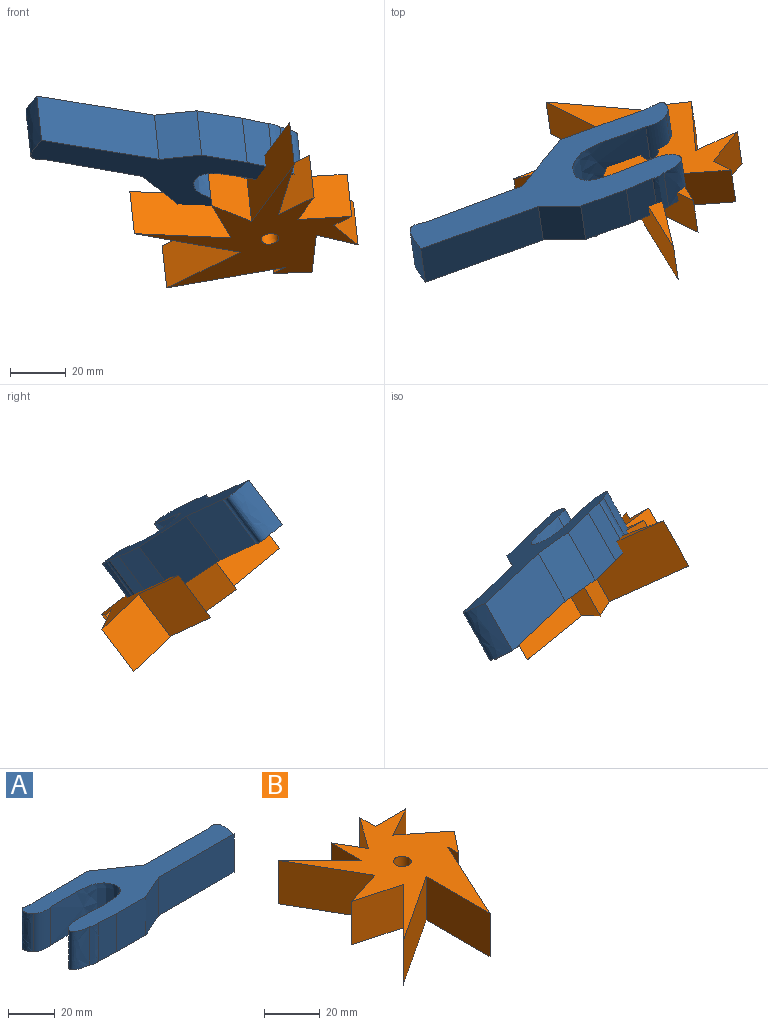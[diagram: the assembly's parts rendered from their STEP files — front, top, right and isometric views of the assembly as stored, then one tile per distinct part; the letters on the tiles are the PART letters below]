
ASSEMBLY  parts=2 mates=1
PART A: 16 faces, bbox 105.6x31.8x20 mm
  f0: extruded ~20x10.45mm, area 209.5mm2, adj f1,f13,f14,f15
  f1: plane 20x17.58mm, normal (0,-1,0), area 351.6mm2, adj f0,f2,f14,f15
  f2: plane 20x14.03mm, normal (0.41,-0.91,0), area 307.4mm2, adj f1,f3,f14,f15
  f3: plane 45.5x20mm, normal (0,-1,0), area 910.1mm2, adj f2,f4,f14,f15
  f4: extruded ~20x11.04mm, area 334.7mm2, adj f3,f5,f14,f15
  f5: plane 37.43x20mm, normal (0.01,1,0), area 748.7mm2, adj f4,f6,f14,f15
  f6: plane 20.32x20mm, normal (0.56,0.83,0), area 490.2mm2, adj f5,f7,f14,f15
  f7: plane 22.22x20mm, normal (0,1,0), area 444.4mm2, adj f6,f8,f14,f15
  f8: extruded ~20x10.59mm, area 212mm2, adj f7,f9,f14,f15
  f9: extruded ~20x2.62mm, area 53.1mm2, adj f8,f10,f14,f15
  f10: extruded ~20x6.43mm, area 224.4mm2, adj f9,f11,f14,f15
  f11: extruded ~20x8.47mm, area 178.4mm2, adj f10,f12,f14,f15
  f12: extruded ~37.73x22.35mm, area 1749.8mm2, adj f11,f13,f14,f15
  f13: extruded ~20x4.6mm, area 94.7mm2, adj f0,f12,f14,f15
  f14: plane 105.56x31.76mm, normal (0,0,1), area 1506.7mm2, adj f0,f1,f2,f3,f4,f5,f6,f7
  f15: plane 105.56x31.76mm, normal (0,0,-1), area 1506.7mm2, adj f0,f1,f2,f3,f4,f5,f6,f7
PART B: 20 faces, bbox 61.5x76.9x19.1 mm
  f0: plane 19.05x17.38mm, normal (-0.3,0.95,0), area 347.6mm2, adj f1,f16,f17,f18
  f1: plane 20.52x19.05mm, normal (-0.27,-0.96,0), area 405.9mm2, adj f0,f2,f17,f18
  f2: plane 25.11x25mm, normal (-0.71,0.71,0), area 675mm2, adj f1,f3,f17,f18
  f3: plane 34.5x22.7mm, normal (0.55,-0.84,0), area 786.8mm2, adj f2,f4,f17,f18
  f4: plane 32.26x19.05mm, normal (-1,0,0), area 614.5mm2, adj f3,f5,f17,f18
  f5: plane 39.64x19.05mm, normal (0.91,-0.42,0), area 832mm2, adj f4,f6,f17,f18
  f6: plane 19.05x5.45mm, normal (-1,0,0), area 103.8mm2, adj f5,f7,f17,f18
  f7: plane 19.05x10.89mm, normal (0.78,-0.62,0), area 265.2mm2, adj f6,f8,f17,f18
  f8: plane 19.05x17.33mm, normal (0.62,0.78,0), area 422mm2, adj f7,f9,f17,f18
  f9: plane 19.05x14.72mm, normal (0.49,-0.87,0), area 320.8mm2, adj f8,f10,f17,f18
  f10: plane 19.05x15.44mm, normal (0,1,0), area 294mm2, adj f9,f11,f17,f18
  f11: plane 19.05x7.87mm, normal (1,0,0), area 149.9mm2, adj f10,f12,f17,f18
  f12: plane 19.05x15.74mm, normal (-0.81,0.59,0), area 370.1mm2, adj f11,f13,f17,f18
  f13: plane 19.05x11.82mm, normal (0.86,0.51,0), area 261.4mm2, adj f12,f14,f17,f18
  f14: plane 19.05x15.53mm, normal (-1,0,0), area 295.8mm2, adj f13,f15,f17,f18
  f15: plane 21.4x21.16mm, normal (0.71,0.7,0), area 573.3mm2, adj f14,f16,f17,f18
  f16: plane 31.05x19.05mm, normal (-0.86,-0.5,0), area 683.8mm2, adj f0,f15,f17,f18
  f17: plane 76.88x61.51mm, normal (0,0,1), area 1595.1mm2, adj f0,f1,f2,f3,f4,f5,f6,f7
  f18: plane 76.88x61.51mm, normal (0,0,-1), area 1595.1mm2, adj f0,f1,f2,f3,f4,f5,f6,f7
  f19: cylinder r=3.17mm len=19.05mm, axis (0,0,1), area 380mm2, adj f17,f18
PLACE A rot(axis=(0.19,-0.93,0.32),178deg) t=(-163.13,-16.66,20.58)mm
PLACE B rot(axis=(0.87,0.48,-0.12),145.2deg) t=(-90.42,16.19,-23.12)mm
MATE cylindrical A.f15 <-> B.f19  axis (0.09,-0.6,-0.8) through (-97.17,-15.85,27.19)mm
